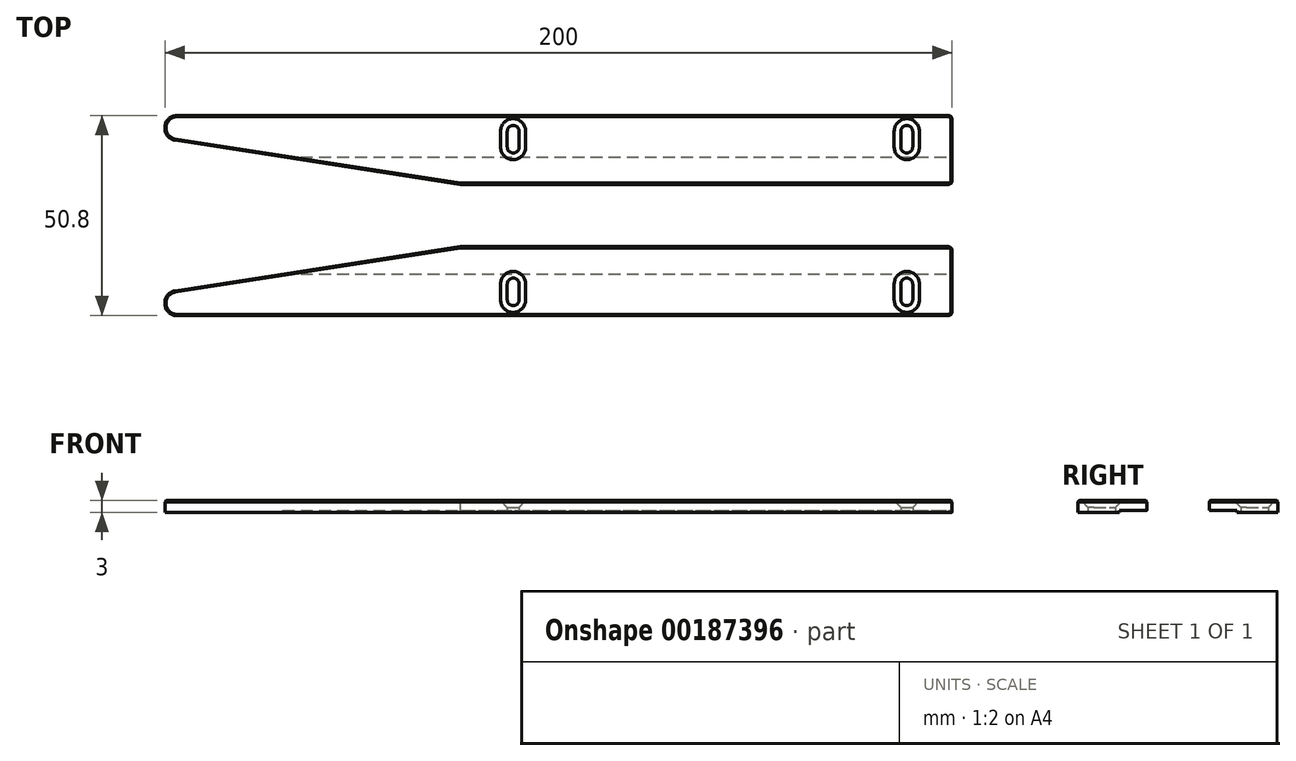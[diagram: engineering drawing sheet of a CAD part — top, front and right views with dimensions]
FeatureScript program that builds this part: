
annotation { "Feature Type Name" : "Feature", "Feature Type Description" : "" }
export const myFeature = defineFeature(function(context is Context, id is Id, definition is map)
    precondition{}
    {
        {
            var Q0;
            Q0=qCreatedBy(makeId("Top.planeOp"),FACE);
            var sketch = newSketch(context, id + "F0", { "sketchPlane" : qUnion([Q0])});
            skLineSegment(sketch, "E0.bottom", {"start": v(0, 0) * mm, "end": v(200, 0) * mm});
            skLineSegment(sketch, "E0.top", {"start": v(0, 17.5) * mm, "end": v(200, 17.5) * mm});
            skLineSegment(sketch, "E0.left", {"start": v(0, 0) * mm, "end": v(0, 17.5) * mm});
            skLineSegment(sketch, "E0.right", {"start": v(200, 0) * mm, "end": v(200, 17.5) * mm});
            skLineSegment(sketch, "E1.bottom", {"start": v(89.97, 4) * mm, "end": v(86.97, 4) * mm});
            skLineSegment(sketch, "E1.top", {"start": v(89.97, 8) * mm, "end": v(86.97, 8) * mm});
            skLineSegment(sketch, "E1.left", {"start": v(89.97, 4) * mm, "end": v(89.97, 8) * mm});
            skLineSegment(sketch, "E1.right", {"start": v(86.97, 4) * mm, "end": v(86.97, 8) * mm});
            skPoint(sketch, "E1.middle", {"position": v(88.47, 6) * mm});
            skLineSegment(sketch, "E2.bottom", {"start": v(189.97, 4) * mm, "end": v(186.97, 4) * mm});
            skLineSegment(sketch, "E2.top", {"start": v(189.97, 8) * mm, "end": v(186.97, 8) * mm});
            skLineSegment(sketch, "E2.left", {"start": v(189.97, 4) * mm, "end": v(189.97, 8) * mm});
            skLineSegment(sketch, "E2.right", {"start": v(186.97, 4) * mm, "end": v(186.97, 8) * mm});
            skPoint(sketch, "E2.middle", {"position": v(188.47, 6) * mm});
            skArc(sketch, "E3", {"start": v(86.97, 8) * mm, "mid": v(88.47, 9.5) * mm, "end": v(89.97, 8) * mm});
            skArc(sketch, "E4", {"start": v(186.97, 8) * mm, "mid": v(188.47, 9.5) * mm, "end": v(189.97, 8) * mm});
            skArc(sketch, "E5", {"start": v(86.97, 4) * mm, "mid": v(88.47, 2.5) * mm, "end": v(89.97, 4) * mm});
            skArc(sketch, "E6", {"start": v(186.97, 4) * mm, "mid": v(188.47, 2.5) * mm, "end": v(189.97, 4) * mm});
            skLineSegment(sketch, "E7", {"start": v(0, 5.85) * mm, "end": v(75.04, 17.5) * mm});
            skSolve(sketch);
        }
        {
            var Q0;
            {var subQ0=sQuery(id+"F0.wireOp",EDGE,"E0.bottom");Q0=makeQuery(id+"F0.imprint","IMPRINT",FACE,{"disambiguationData":[TD([[makeQuery(id+"F0.imprint","IMPRINT",EDGE,{"derivedFrom":subQ0}),1.0]])]});}
            extrude(context, id + "F1", {"entities" : qUnion([Q0]), "depth" : 3 * mm});
        }
        {
            var Q0;
            Q0=makeQuery(id+"F1.opExtrude","SWEPT_FACE",FACE,{"disambiguationData":[OSD([sQuery(id+"F0.wireOp",EDGE,"E0.right")])]});
            var sketch = newSketch(context, id + "F2", { "sketchPlane" : qUnion([Q0])});
            skLineSegment(sketch, "E8.bottom", {"start": v(17.5, 0) * mm, "end": v(10.5, 0) * mm});
            skLineSegment(sketch, "E8.top", {"start": v(17.5, 0.5) * mm, "end": v(10.5, 0.5) * mm});
            skLineSegment(sketch, "E8.left", {"start": v(17.5, 0) * mm, "end": v(17.5, 0.5) * mm});
            skLineSegment(sketch, "E8.right", {"start": v(10.5, 0) * mm, "end": v(10.5, 0.5) * mm});
            skSolve(sketch);
        }
        {
            var Q0;
            Q0=makeQuery(id+"F2.imprint","IMPRINT",FACE,{"disambiguationData":[TD([[makeQuery(id+"F2.imprint","IMPRINT",EDGE,{"derivedFrom":sQuery(id+"F2.wireOp",EDGE,"E8.bottom")}),1.0]])]});
            extrude(context, id + "F3", {"entities" : qUnion([Q0]), "operationType" : NewBodyOperationType.REMOVE, "endBound" : BoundingType.THROUGH_ALL, "oppositeDirection" : true, "depth" : 25.4 * mm});
        }
        {
            var Q0;
            Q0=makeQuery(id+"F1.opExtrude","SWEPT_FACE",FACE,{"disambiguationData":[OSD([sQuery(id+"F0.wireOp",EDGE,"E0.bottom")])]});
            cPlane(context, id + "F4", {"entities" : qUnion([Q0]), "cplaneType" : CPlaneType.OFFSET, "offset" : 25.4 * mm, "oppositeDirection" : true, "width" : 152.4 * mm, "height" : 152.4 * mm});
        }
        {
            var Q0;
            Q0=makeQuery(id+"F1.opExtrude","SWEPT_BODY",BODY,{"disambiguationData":[OSD([sQuery(id+"F0.wireOp",EDGE,"E0.bottom"),sQuery(id+"F0.wireOp",EDGE,"E0.top"),sQuery(id+"F0.wireOp",EDGE,"E0.left"),sQuery(id+"F0.wireOp",EDGE,"E0.right"),sQuery(id+"F0.wireOp",EDGE,"E1.left"),sQuery(id+"F0.wireOp",EDGE,"E1.right"),sQuery(id+"F0.wireOp",EDGE,"E2.left"),sQuery(id+"F0.wireOp",EDGE,"E2.right"),sQuery(id+"F0.wireOp",EDGE,"E3"),sQuery(id+"F0.wireOp",EDGE,"E4"),sQuery(id+"F0.wireOp",EDGE,"E5"),sQuery(id+"F0.wireOp",EDGE,"E6"),sQuery(id+"F0.wireOp",EDGE,"EhPgQ6kI-HOte-GhGe-7i3y-vseyqDZMkckJ")])]});
            var Q1;
            Q1=qCreatedBy(id+"F4.planeOp",FACE);
            mirror(context, id + "F5", {"entities" : qUnion([Q0]), "mirrorPlane" : qUnion([Q1])});
        }
        {
            var Q0;
            Q0=makeQuery(id+"F1.opExtrude","SWEPT_EDGE",EDGE,{"disambiguationData":[OSD([sQuery(id+"F0.wireOp",EDGE,"E0.left"),sQuery(id+"F0.wireOp",EDGE,"EhPgQ6kI-HOte-GhGe-7i3y-vseyqDZMkckJ")])]});
            fillet(context, id + "F6", {"entities" : qUnion([Q0]), "radius" : 3 * mm, "tangentPropagation" : true, "allowEdgeOverflow" : false});
        }
        {
            var Q0;
            Q0=makeQuery(id+"F5.opPattern","COPY",EDGE,{"derivedFrom":makeQuery(id+"F1.opExtrude","SWEPT_EDGE",EDGE,{"disambiguationData":[OSD([sQuery(id+"F0.wireOp",EDGE,"E0.left"),sQuery(id+"F0.wireOp",EDGE,"EhPgQ6kI-HOte-GhGe-7i3y-vseyqDZMkckJ")])]}),"instanceName":"1"});
            fillet(context, id + "F7", {"entities" : qUnion([Q0]), "radius" : 3 * mm, "tangentPropagation" : true, "allowEdgeOverflow" : false});
        }
        {
            var Q0;
            Q0=makeQuery(id+"F1.opExtrude","SWEPT_EDGE",EDGE,{"disambiguationData":[OSD([sQuery(id+"F0.wireOp",EDGE,"E0.bottom"),sQuery(id+"F0.wireOp",EDGE,"E0.right")])]});
            var Q1;
            Q1=makeQuery(id+"F5.opPattern","COPY",EDGE,{"derivedFrom":makeQuery(id+"F1.opExtrude","SWEPT_EDGE",EDGE,{"disambiguationData":[OSD([sQuery(id+"F0.wireOp",EDGE,"E0.bottom"),sQuery(id+"F0.wireOp",EDGE,"E0.right")])]}),"instanceName":"1"});
            var Q2;
            Q2=makeQuery(id+"F1.opExtrude","SWEPT_EDGE",EDGE,{"disambiguationData":[OSD([sQuery(id+"F0.wireOp",EDGE,"E0.top"),sQuery(id+"F0.wireOp",EDGE,"E0.right")])]});
            var Q3;
            Q3=makeQuery(id+"F5.opPattern","COPY",EDGE,{"derivedFrom":makeQuery(id+"F1.opExtrude","SWEPT_EDGE",EDGE,{"disambiguationData":[OSD([sQuery(id+"F0.wireOp",EDGE,"E0.top"),sQuery(id+"F0.wireOp",EDGE,"E0.right")])]}),"instanceName":"1"});
            fillet(context, id + "F8", {"entities" : qUnion([Q0, Q1, Q2, Q3]), "radius" : 1 * mm, "tangentPropagation" : true, "allowEdgeOverflow" : false});
        }
        {
            var Q0;
            Q0=makeQuery(id+"F1.opExtrude","CAP_EDGE",EDGE,{"disambiguationData":[OSD([sQuery(id+"F0.wireOp",EDGE,"E0.top")])],"isStart":false});
            var Q1;
            Q1=makeQuery(id+"F1.opExtrude","CAP_EDGE",EDGE,{"disambiguationData":[OSD([sQuery(id+"F0.wireOp",EDGE,"EhPgQ6kI-HOte-GhGe-7i3y-vseyqDZMkckJ")])],"isStart":false});
            var Q2;
            Q2=makeQuery(id+"F5.opPattern","COPY",EDGE,{"derivedFrom":makeQuery(id+"F1.opExtrude","CAP_EDGE",EDGE,{"disambiguationData":[OSD([sQuery(id+"F0.wireOp",EDGE,"E0.top")])],"isStart":false}),"instanceName":"1"});
            var Q3;
            Q3=makeQuery(id+"F5.opPattern","COPY",EDGE,{"derivedFrom":makeQuery(id+"F1.opExtrude","CAP_EDGE",EDGE,{"disambiguationData":[OSD([sQuery(id+"F0.wireOp",EDGE,"EhPgQ6kI-HOte-GhGe-7i3y-vseyqDZMkckJ")])],"isStart":false}),"instanceName":"1"});
            chamfer(context, id + "F9", {"entities" : qUnion([Q0, Q1, Q2, Q3]), "width" : .3 * mm, "tangentPropagation" : true});
        }
        {
            var Q0;
            Q0=makeQuery(id+"F1.opExtrude","CAP_EDGE",EDGE,{"disambiguationData":[OSD([sQuery(id+"F0.wireOp",EDGE,"E1.left")])],"isStart":false});
            var Q1;
            Q1=makeQuery(id+"F1.opExtrude","CAP_EDGE",EDGE,{"disambiguationData":[OSD([sQuery(id+"F0.wireOp",EDGE,"E3")])],"isStart":false});
            var Q2;
            Q2=makeQuery(id+"F1.opExtrude","CAP_EDGE",EDGE,{"disambiguationData":[OSD([sQuery(id+"F0.wireOp",EDGE,"E1.right")])],"isStart":false});
            var Q3;
            Q3=makeQuery(id+"F1.opExtrude","CAP_EDGE",EDGE,{"disambiguationData":[OSD([sQuery(id+"F0.wireOp",EDGE,"E5")])],"isStart":false});
            var Q4;
            Q4=makeQuery(id+"F1.opExtrude","CAP_EDGE",EDGE,{"disambiguationData":[OSD([sQuery(id+"F0.wireOp",EDGE,"E4")])],"isStart":false});
            var Q5;
            Q5=makeQuery(id+"F1.opExtrude","CAP_EDGE",EDGE,{"disambiguationData":[OSD([sQuery(id+"F0.wireOp",EDGE,"E2.left")])],"isStart":false});
            var Q6;
            Q6=makeQuery(id+"F1.opExtrude","CAP_EDGE",EDGE,{"disambiguationData":[OSD([sQuery(id+"F0.wireOp",EDGE,"E6")])],"isStart":false});
            var Q7;
            Q7=makeQuery(id+"F1.opExtrude","CAP_EDGE",EDGE,{"disambiguationData":[OSD([sQuery(id+"F0.wireOp",EDGE,"E2.right")])],"isStart":false});
            var Q8;
            Q8=makeQuery(id+"F5.opPattern","COPY",EDGE,{"derivedFrom":makeQuery(id+"F1.opExtrude","CAP_EDGE",EDGE,{"disambiguationData":[OSD([sQuery(id+"F0.wireOp",EDGE,"E2.left")])],"isStart":false}),"instanceName":"1"});
            var Q9;
            Q9=makeQuery(id+"F5.opPattern","COPY",EDGE,{"derivedFrom":makeQuery(id+"F1.opExtrude","CAP_EDGE",EDGE,{"disambiguationData":[OSD([sQuery(id+"F0.wireOp",EDGE,"E4")])],"isStart":false}),"instanceName":"1"});
            var Q10;
            Q10=makeQuery(id+"F5.opPattern","COPY",EDGE,{"derivedFrom":makeQuery(id+"F1.opExtrude","CAP_EDGE",EDGE,{"disambiguationData":[OSD([sQuery(id+"F0.wireOp",EDGE,"E2.right")])],"isStart":false}),"instanceName":"1"});
            var Q11;
            Q11=makeQuery(id+"F5.opPattern","COPY",EDGE,{"derivedFrom":makeQuery(id+"F1.opExtrude","CAP_EDGE",EDGE,{"disambiguationData":[OSD([sQuery(id+"F0.wireOp",EDGE,"E6")])],"isStart":false}),"instanceName":"1"});
            var Q12;
            Q12=makeQuery(id+"F5.opPattern","COPY",EDGE,{"derivedFrom":makeQuery(id+"F1.opExtrude","CAP_EDGE",EDGE,{"disambiguationData":[OSD([sQuery(id+"F0.wireOp",EDGE,"E5")])],"isStart":false}),"instanceName":"1"});
            var Q13;
            Q13=makeQuery(id+"F5.opPattern","COPY",EDGE,{"derivedFrom":makeQuery(id+"F1.opExtrude","CAP_EDGE",EDGE,{"disambiguationData":[OSD([sQuery(id+"F0.wireOp",EDGE,"E1.left")])],"isStart":false}),"instanceName":"1"});
            var Q14;
            Q14=makeQuery(id+"F5.opPattern","COPY",EDGE,{"derivedFrom":makeQuery(id+"F1.opExtrude","CAP_EDGE",EDGE,{"disambiguationData":[OSD([sQuery(id+"F0.wireOp",EDGE,"E3")])],"isStart":false}),"instanceName":"1"});
            var Q15;
            Q15=makeQuery(id+"F5.opPattern","COPY",EDGE,{"derivedFrom":makeQuery(id+"F1.opExtrude","CAP_EDGE",EDGE,{"disambiguationData":[OSD([sQuery(id+"F0.wireOp",EDGE,"E1.right")])],"isStart":false}),"instanceName":"1"});
            chamfer(context, id + "F10", {"entities" : qUnion([Q0, Q1, Q2, Q3, Q4, Q5, Q6, Q7, Q8, Q9, Q10, Q11, Q12, Q13, Q14, Q15]), "chamferType" : ChamferType.OFFSET_ANGLE, "width" : 1.7 * mm, "oppositeDirection" : false, "angle" : 45 * degree, "tangentPropagation" : true});
        }
    });
